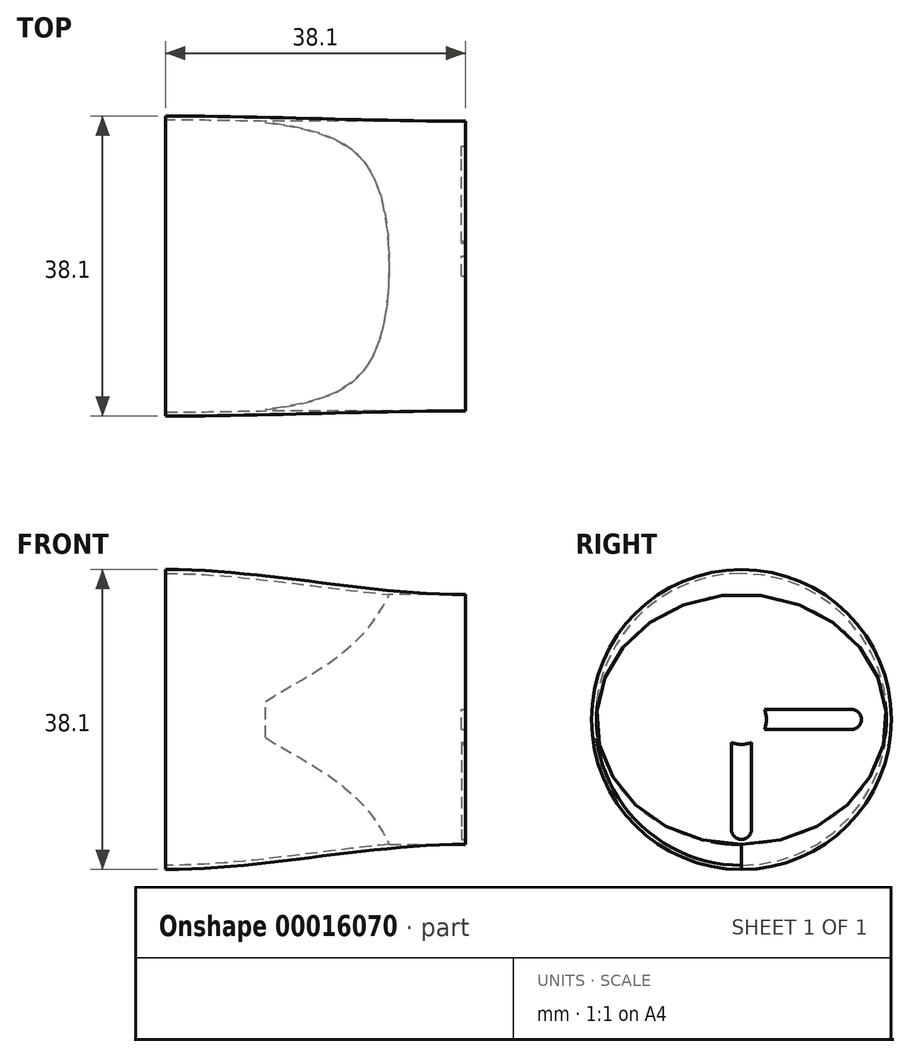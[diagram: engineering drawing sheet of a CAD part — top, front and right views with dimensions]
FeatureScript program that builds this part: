
annotation { "Feature Type Name" : "Feature", "Feature Type Description" : "" }
export const myFeature = defineFeature(function(context is Context, id is Id, definition is map)
    precondition{}
    {
        {
            var Q0;
            Q0=qCreatedBy(makeId("Right.planeOp"),FACE);
            var sketch = newSketch(context, id + "F0", { "sketchPlane" : qUnion([Q0])});
            skCircle(sketch, "E0", {"center": v(0, 0) * mm, "radius": 19.05 * mm});
            skSolve(sketch);
        }
        {
            var Q0;
            Q0=qCreatedBy(makeId("Right.planeOp"),FACE);
            cPlane(context, id + "F1", {"entities" : qUnion([Q0]), "cplaneType" : CPlaneType.OFFSET, "offset" : 38.1 * mm, "width" : 152.4 * mm, "height" : 152.4 * mm});
        }
        {
            var Q0;
            Q0=qCreatedBy(id+"F1.planeOp",FACE);
            var sketch = newSketch(context, id + "F2", { "sketchPlane" : qUnion([Q0])});
            skEllipse(sketch, "E1", {"center": v(0, 0) * mm, "majorRadius": 18.41 * mm, "minorRadius": 15.88 * mm, "majorAxis": v(1, 0)});
            skSolve(sketch);
        }
        {
            var Q0;
            Q0=makeQuery(id+"F0.imprint","IMPRINT",FACE,{"disambiguationData":[TD([[makeQuery(id+"F0.imprint","IMPRINT",EDGE,{"derivedFrom":sQuery(id+"F0.wireOp",EDGE,"E0")}),1.0]])]});
            var Q1;
            Q1=makeQuery(id+"F2.imprint","IMPRINT",FACE,{"disambiguationData":[TD([[makeQuery(id+"F2.imprint","IMPRINT",EDGE,{"derivedFrom":sQuery(id+"F2.wireOp",EDGE,"E1")}),1.0]])]});
            loft(context, id + "F3", {"startCondition" : LoftEndDerivativeType.NORMAL_TO_PROFILE, "startMagnitude" : 1, "endCondition" : LoftEndDerivativeType.NORMAL_TO_PROFILE, "endMagnitude" : 1, "sheetProfilesArray" : [{ "sheetProfileEntities" : qUnion([Q0]) }, { "sheetProfileEntities" : qUnion([Q1]) }]});
        }
        {
            var Q0;
            Q0=makeQuery(id+"F3.opLoft","CAP_FACE",FACE,{"disambiguationData":[OSD([makeQuery(id+"F0.imprint","IMPRINT",FACE,{"disambiguationData":[TD([[makeQuery(id+"F0.imprint","IMPRINT",EDGE,{"derivedFrom":sQuery(id+"F0.wireOp",EDGE,"E0")}),1.0]])]})])],"isStart":true});
            shell(context, id + "F4", {"entities" : qUnion([Q0]), "thickness" : 0.5 * mm});
        }
        {
            var Q0;
            Q0=makeQuery(id+"F3.opLoft","CAP_FACE",FACE,{"disambiguationData":[OSD([makeQuery(id+"F2.imprint","IMPRINT",FACE,{"disambiguationData":[TD([[makeQuery(id+"F2.imprint","IMPRINT",EDGE,{"derivedFrom":sQuery(id+"F2.wireOp",EDGE,"E1")}),1.0]])]})])],"isStart":true});
            var sketch = newSketch(context, id + "F5", { "sketchPlane" : qUnion([Q0])});
            skCircle(sketch, "E2", {"center": v(0, 0) * mm, "radius": 3.18 * mm});
            skLineSegment(sketch, "E3.top", {"start": v(0, -1.27) * mm, "end": v(-13.97, -1.27) * mm});
            skLineSegment(sketch, "E3.left", {"start": v(0, 0) * mm, "end": v(0, -1.27) * mm});
            skLineSegment(sketch, "E4.top", {"start": v(0, 1.27) * mm, "end": v(-13.97, 1.27) * mm});
            skLineSegment(sketch, "E4.left", {"start": v(0, 0) * mm, "end": v(0, 1.27) * mm});
            skArc(sketch, "E5", {"start": v(-13.97, 1.27) * mm, "mid": v(-15.24, 0) * mm, "end": v(-13.97, -1.27) * mm});
            skLineSegment(sketch, "E6.MirrorCS", {"start": v(0, 1.27) * mm, "end": v(13.97, 1.27) * mm});
            skArc(sketch, "E7.MirrorCS", {"start": v(13.97, 1.27) * mm, "mid": v(15.24, 0) * mm, "end": v(13.97, -1.27) * mm});
            skLineSegment(sketch, "E8.MirrorCS", {"start": v(0, -1.27) * mm, "end": v(13.97, -1.27) * mm});
            skLineSegment(sketch, "E9", {"start": v(0, 0) * mm, "end": v(-1.27, 0) * mm});
            skLineSegment(sketch, "E10", {"start": v(-1.27, 0) * mm, "end": v(-1.27, 13.97) * mm});
            skLineSegment(sketch, "E11", {"start": v(-1.27, 13.97) * mm, "end": v(1.27, 13.97) * mm});
            skLineSegment(sketch, "E12", {"start": v(1.27, 13.97) * mm, "end": v(1.27, 0) * mm});
            skArc(sketch, "E13", {"start": v(1.27, 13.97) * mm, "mid": v(0, 15.24) * mm, "end": v(-1.27, 13.97) * mm});
            skLineSegment(sketch, "E14.MirrorCS", {"start": v(-1.27, 0) * mm, "end": v(-1.27, -13.97) * mm});
            skLineSegment(sketch, "E15.MirrorCS", {"start": v(1.27, -13.97) * mm, "end": v(1.27, 0) * mm});
            skArc(sketch, "E16.MirrorCS", {"start": v(1.27, -13.97) * mm, "mid": v(0, -15.24) * mm, "end": v(-1.27, -13.97) * mm});
            skSolve(sketch);
        }
        {
            var Q0;
            {var subQ3=sQuery(id+"F5.wireOp",EDGE,"E11");Q0=makeQuery(id+"F5.imprint","IMPRINT",FACE,{"disambiguationData":[TD([[makeQuery(id+"F5.imprint","IMPRINT",EDGE,{"derivedFrom":subQ3}),-1.0]])]});}
            var Q1;
            Q1=makeQuery(id+"F5.imprint","IMPRINT",FACE,{"disambiguationData":[TD([[makeQuery(id+"F5.imprint","IMPRINT",EDGE,{"derivedFrom":sQuery(id+"F5.wireOp",EDGE,"E11")}),1.0]])]});
            var Q2;
            {var subQ3=sQuery(id+"F5.wireOp",EDGE,"E7.MirrorCS");Q2=makeQuery(id+"F5.imprint","IMPRINT",FACE,{"disambiguationData":[TD([[makeQuery(id+"F5.imprint","IMPRINT",EDGE,{"derivedFrom":subQ3}),-1.0]])]});}
            var Q3;
            {var subQ0=sQuery(id+"F5.wireOp",EDGE,"E5");Q3=makeQuery(id+"F5.imprint","IMPRINT",FACE,{"disambiguationData":[TD([[makeQuery(id+"F5.imprint","IMPRINT",EDGE,{"derivedFrom":subQ0}),1.0]])]});}
            var Q4;
            {var subQ3=sQuery(id+"F5.wireOp",EDGE,"E16.MirrorCS");Q4=makeQuery(id+"F5.imprint","IMPRINT",FACE,{"disambiguationData":[TD([[makeQuery(id+"F5.imprint","IMPRINT",EDGE,{"derivedFrom":subQ3}),-1.0]])]});}
            var Q5;
            {var subQ5=sQuery(id+"F5.wireOp",EDGE,"E4.top");var subQ7=sQuery(id+"F5.wireOp",EDGE,"E2");var subQ9=makeQuery(id+"F5.imprint","INTERSECT",VERTEX,{"derivedFrom":[subQ7,subQ5]});Q5=makeQuery(id+"F5.imprint","IMPRINT",FACE,{"disambiguationData":[TD([[makeQuery(id+"F5.imprint","IMPRINT",EDGE,{"disambiguationData":[TD([[subQ9,-1.0]])],"derivedFrom":subQ7}),1.0]])]});}
            var Q6;
            {var subQ0=sQuery(id+"F5.wireOp",EDGE,"E10");var subQ3=sQuery(id+"F5.wireOp",EDGE,"E2");var subQ4=makeQuery(id+"F5.imprint","INTERSECT",VERTEX,{"derivedFrom":[subQ3,subQ0]});Q6=makeQuery(id+"F5.imprint","IMPRINT",FACE,{"disambiguationData":[TD([[makeQuery(id+"F5.imprint","IMPRINT",EDGE,{"disambiguationData":[TD([[subQ4,-1.0]])],"derivedFrom":subQ3}),1.0]])]});}
            var Q7;
            {var subQ0=sQuery(id+"F5.wireOp",EDGE,"E12");var subQ3=sQuery(id+"F5.wireOp",EDGE,"E2");var subQ4=makeQuery(id+"F5.imprint","INTERSECT",VERTEX,{"derivedFrom":[subQ3,subQ0]});Q7=makeQuery(id+"F5.imprint","IMPRINT",FACE,{"disambiguationData":[TD([[makeQuery(id+"F5.imprint","IMPRINT",EDGE,{"disambiguationData":[TD([[subQ4,-1.0]])],"derivedFrom":subQ3}),1.0]])]});}
            var Q8;
            {var subQ0=sQuery(id+"F5.wireOp",EDGE,"E12");var subQ3=sQuery(id+"F5.wireOp",EDGE,"E2");var subQ4=makeQuery(id+"F5.imprint","INTERSECT",VERTEX,{"derivedFrom":[subQ3,subQ0]});Q8=makeQuery(id+"F5.imprint","IMPRINT",FACE,{"disambiguationData":[TD([[makeQuery(id+"F5.imprint","IMPRINT",EDGE,{"disambiguationData":[TD([[subQ4,1.0]])],"derivedFrom":subQ3}),1.0]])]});}
            var Q9;
            {var subQ5=sQuery(id+"F5.wireOp",EDGE,"E6.MirrorCS");var subQ7=sQuery(id+"F5.wireOp",EDGE,"E2");var subQ9=makeQuery(id+"F5.imprint","INTERSECT",VERTEX,{"derivedFrom":[subQ7,subQ5]});Q9=makeQuery(id+"F5.imprint","IMPRINT",FACE,{"disambiguationData":[TD([[makeQuery(id+"F5.imprint","IMPRINT",EDGE,{"disambiguationData":[TD([[subQ9,1.0]])],"derivedFrom":subQ7}),1.0]])]});}
            var Q10;
            {var subQ0=sQuery(id+"F5.wireOp",EDGE,"E15.MirrorCS");var subQ3=sQuery(id+"F5.wireOp",EDGE,"E2");var subQ4=makeQuery(id+"F5.imprint","INTERSECT",VERTEX,{"derivedFrom":[subQ3,subQ0]});Q10=makeQuery(id+"F5.imprint","IMPRINT",FACE,{"disambiguationData":[TD([[makeQuery(id+"F5.imprint","IMPRINT",EDGE,{"disambiguationData":[TD([[subQ4,-1.0]])],"derivedFrom":subQ3}),1.0]])]});}
            var Q11;
            {var subQ3=sQuery(id+"F5.wireOp",EDGE,"E2");var subQ5=sQuery(id+"F5.wireOp",EDGE,"E14.MirrorCS");var subQ8=makeQuery(id+"F5.imprint","INTERSECT",VERTEX,{"derivedFrom":[subQ3,subQ5]});Q11=makeQuery(id+"F5.imprint","IMPRINT",FACE,{"disambiguationData":[TD([[makeQuery(id+"F5.imprint","IMPRINT",EDGE,{"disambiguationData":[TD([[subQ8,-1.0]])],"derivedFrom":subQ3}),1.0]])]});}
            var Q12;
            {var subQ1=sQuery(id+"F5.wireOp",EDGE,"E3.top");var subQ3=sQuery(id+"F5.wireOp",EDGE,"E2");var subQ5=makeQuery(id+"F5.imprint","INTERSECT",VERTEX,{"derivedFrom":[subQ3,subQ1]});Q12=makeQuery(id+"F5.imprint","IMPRINT",FACE,{"disambiguationData":[TD([[makeQuery(id+"F5.imprint","IMPRINT",EDGE,{"disambiguationData":[TD([[subQ5,-1.0]])],"derivedFrom":subQ3}),1.0]])]});}
            var Q13;
            {var subQ4=sQuery(id+"F5.wireOp",EDGE,"E3.left");Q13=makeQuery(id+"F5.imprint","IMPRINT",FACE,{"disambiguationData":[TD([[makeQuery(id+"F5.imprint","IMPRINT",EDGE,{"derivedFrom":subQ4}),-1.0]])]});}
            var Q14;
            {var subQ4=sQuery(id+"F5.wireOp",EDGE,"E4.left");Q14=makeQuery(id+"F5.imprint","IMPRINT",FACE,{"disambiguationData":[TD([[makeQuery(id+"F5.imprint","IMPRINT",EDGE,{"derivedFrom":subQ4}),1.0]])]});}
            var Q15;
            {var subQ8=sQuery(id+"F5.wireOp",EDGE,"E3.left");Q15=makeQuery(id+"F5.imprint","IMPRINT",FACE,{"disambiguationData":[TD([[makeQuery(id+"F5.imprint","IMPRINT",EDGE,{"derivedFrom":subQ8}),1.0]])]});}
            extrude(context, id + "F6", {"entities" : qUnion([Q0, Q1, Q2, Q3, Q4, Q5, Q6, Q7, Q8, Q9, Q10, Q11, Q12, Q13, Q14, Q15]), "operationType" : NewBodyOperationType.REMOVE, "oppositeDirection" : true, "depth" : 25.4 * mm});
        }
    });
